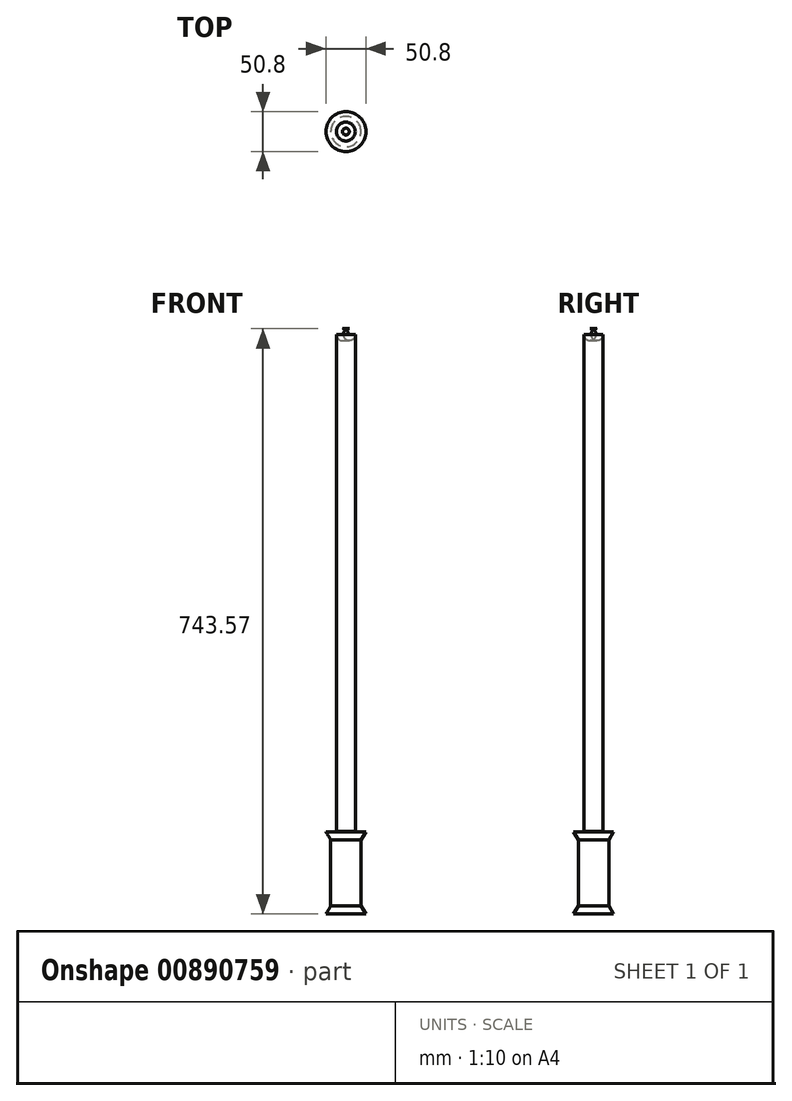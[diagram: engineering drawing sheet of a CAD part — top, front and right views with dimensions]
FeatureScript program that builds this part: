
annotation { "Feature Type Name" : "Feature", "Feature Type Description" : "" }
export const myFeature = defineFeature(function(context is Context, id is Id, definition is map)
    precondition{}
    {
        {
            var Q0;
            Q0=qCreatedBy(makeId("Front.planeOp"),FACE);
            var sketch = newSketch(context, id + "F0", { "sketchPlane" : qUnion([Q0])});
            skLineSegment(sketch, "E0.bottom", {"start": v(0, -45.1) * mm, "end": v(-19.24, -45.1) * mm});
            skLineSegment(sketch, "E0.top", {"start": v(0, 38.95) * mm, "end": v(-19.24, 38.95) * mm});
            skLineSegment(sketch, "E0.left", {"start": v(0, -45.1) * mm, "end": v(0, 38.95) * mm});
            skLineSegment(sketch, "E0.right", {"start": v(-19.24, -45.1) * mm, "end": v(-19.24, 38.95) * mm});
            skLineSegment(sketch, "E1", {"start": v(-19.24, -45.1) * mm, "end": v(-25.4, -55.26) * mm});
            skLineSegment(sketch, "E2", {"start": v(-25.4, -55.26) * mm, "end": v(0, -55.26) * mm});
            skLineSegment(sketch, "E3", {"start": v(0, -55.26) * mm, "end": v(0, -45.1) * mm});
            skLineSegment(sketch, "E4", {"start": v(0, 38.95) * mm, "end": v(0, 49.1) * mm});
            skLineSegment(sketch, "E5", {"start": v(-19.24, 38.95) * mm, "end": v(-25.4, 49.1) * mm});
            skLineSegment(sketch, "E6", {"start": v(-25.4, 49.1) * mm, "end": v(0, 49.1) * mm});
            skSolve(sketch);
        }
        {
            var Q0;
            Q0=makeQuery(id+"F0.imprint","IMPRINT",FACE,{"disambiguationData":[TD([[makeQuery(id+"F0.imprint","IMPRINT",EDGE,{"derivedFrom":sQuery(id+"F0.wireOp",EDGE,"E0.top")}),-1.0]])]});
            var Q1;
            Q1=makeQuery(id+"F0.imprint","IMPRINT",FACE,{"disambiguationData":[TD([[makeQuery(id+"F0.imprint","IMPRINT",EDGE,{"derivedFrom":sQuery(id+"F0.wireOp",EDGE,"E0.bottom")}),1.0]])]});
            var Q2;
            Q2=makeQuery(id+"F0.imprint","IMPRINT",FACE,{"disambiguationData":[TD([[makeQuery(id+"F0.imprint","IMPRINT",EDGE,{"derivedFrom":sQuery(id+"F0.wireOp",EDGE,"E0.bottom")}),-1.0]])]});
            var Q3;
            Q3=sQuery(id+"F0.wireOp",EDGE,"E3");
            revolve(context, id + "F1", {"surfaceOperationType" : NewSurfaceOperationType.NEW, "entities" : qUnion([Q0, Q1, Q2]), "axis" : qUnion([Q3]), "revolveType" : RevolveType.FULL});
        }
        {
            var Q0;
            Q0=qCreatedBy(makeId("Right.planeOp"),FACE);
            var sketch = newSketch(context, id + "F2", { "sketchPlane" : qUnion([Q0])});
            skLineSegment(sketch, "E7.bottom", {"start": v(0, 49.93) * mm, "end": v(11.94, 49.93) * mm});
            skLineSegment(sketch, "E7.top", {"start": v(0, 78.71) * mm, "end": v(11.94, 78.71) * mm});
            skLineSegment(sketch, "E7.left", {"start": v(0, 49.93) * mm, "end": v(0, 78.71) * mm});
            skLineSegment(sketch, "E7.right", {"start": v(11.94, 49.93) * mm, "end": v(11.94, 78.71) * mm});
            skSolve(sketch);
        }
        {
            var Q0;
            Q0=makeQuery(id+"F2.imprint","IMPRINT",FACE,{"disambiguationData":[TD([[makeQuery(id+"F2.imprint","IMPRINT",EDGE,{"derivedFrom":sQuery(id+"F2.wireOp",EDGE,"E7.bottom")}),1.0]])]});
            var Q1;
            Q1=sQuery(id+"F2.wireOp",EDGE,"E7.left");
            revolve(context, id + "F3", {"surfaceOperationType" : NewSurfaceOperationType.NEW, "entities" : qUnion([Q0]), "axis" : qUnion([Q1]), "revolveType" : RevolveType.FULL});
        }
        {
            var Q0;
            Q0=makeQuery(id+"F3.opRevolve","SWEPT_FACE",FACE,{"disambiguationData":[OSD([sQuery(id+"F2.wireOp",EDGE,"E7.top")])]});
            extrude(context, id + "F4", {"entities" : qUnion([Q0]), "operationType" : NewBodyOperationType.ADD, "depth" : 609.6 * mm, "offsetDistance" : 25.4 * mm});
        }
        {
            var Q0;
            Q0=makeQuery(id+"F4.opExtrude","CAP_EDGE",EDGE,{"disambiguationData":[OSD([sQuery(id+"F2.wireOp",EDGE,"E7.top"),sQuery(id+"F2.wireOp",EDGE,"E7.right")])],"isStart":false});
            fillet(context, id + "F5", {"entities" : qUnion([Q0]), "radius" : 7.62 * mm, "tangentPropagation" : true, "allowEdgeOverflow" : false});
        }
    });
